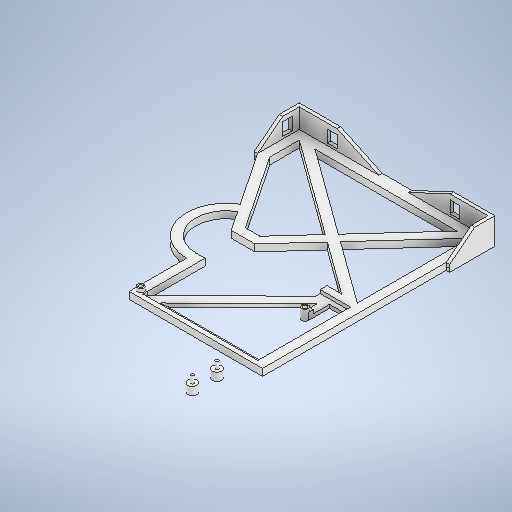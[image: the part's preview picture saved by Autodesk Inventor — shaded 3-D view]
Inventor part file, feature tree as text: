
AUTODESK INVENTOR PART (.ipt)
format: ipt  version: 2025.2 (Build 292293000, 293)  size: 659,968 bytes
history: native  units: mm
features: extrude x17, sketch x5
ambient origin geometry x8: Origin, YZ Plane, XZ Plane, XY Plane, X Axis, Y Axis, Z Axis, Center Point
bodies: Solid1 (feature_tree)
feature tree (22):
  sketch  "Sketch1"  dims[d0=82.0mm d1=54.0mm]
  extrude  "Extrusion1"  Depth=54.0mm
  extrude  "Extrusion2"  Depth=3.0mm
  extrude  "Extrusion3"  Depth=2.9mm
  extrude  "Extrusion4"  Depth=1.5mm TaperAngle=0.0deg
  extrude  "Extrusion5"  Depth=12.24mm
  extrude  "Extrusion6"  Depth=4.2mm
  extrude  "Extrusion10"  Depth=5.2mm
  sketch  "Sketch16"  dims[d6=2.9mm d8=12.5mm]
  extrude  "Extrusion11"  Depth=1.0mm
  extrude  "Extrusion12"  Depth=1.5mm TaperAngle=0.0deg
  extrude  "Extrusion13"  Depth=1.5mm TaperAngle=0.0deg
  extrude  "Extrusion14"  Depth=1.5mm TaperAngle=0.0deg
  extrude  "Extrusion15"  Depth=4.5mm
  extrude  "Extrusion16"  Depth=4.5mm
  extrude  "Extrusion17"  Depth=5.5mm
  extrude  "Extrusion18"  Depth=1.0mm
  extrude  "Extrusion19"  Depth=0.5mm
  extrude  "Extrusion20"  Depth=1.5mm TaperAngle=0.0deg
  sketch  "Sketch2"  dims[d2=44.0mm d5=3.0mm]
  sketch  "Sketch25"  dims[d9=2.9mm d10=1.5mm d11=0.0mm]
  sketch  "Sketch26"  dims[d13=10.0mm d14=12.24mm d16=4.2mm d17=5.2mm d18=1.0mm d19=1.5mm d20=0.0mm d22=1.5mm d23=0.0mm d24=1.5mm d25=0.0mm d26=4.5mm d27=4.5mm d28=5.5mm d29=1.0mm d30=13.825495mm d31=1.5mm d32=0.0mm d34=20.0mm d35=16.44mm d36=18.104mm d37=3.0mm d38=0.0mm d76=1.7mm d78=0.0mm d79=0.0mm d80=4.0mm d81=1.3mm d83=2.0mm d84=0.0mm d85=2.0mm d86=0.0mm d87=5.0mm d88=0.0mm d94=90.0deg d95=90.0deg d96=31.0mm d97=4.0mm d98=4.0mm d103=4.0mm d104=4.0mm d105=1.5mm d106=0.0mm d107=1.5mm d108=0.0mm d110=1.8mm d112=4.0mm d113=7.765622mm d114=1.5mm d115=0.0mm d121=23.473586mm d122=23.650304mm d123=13.528693mm d124=13.140289mm d125=90.0deg d126=9.427875mm d127=7.403962mm d128=4.0mm d129=4.0mm d130=25.52254mm d131=11.748234mm d132=25.0mm d133=51.672948mm d134=4.0mm d135=7.2mm d136=1.5mm d137=1.5mm d138=1.5mm d139=0.0mm d140=2.0mm d141=17.152547mm d142=2.0mm d143=7.942341mm d144=7.0mm d146=1.5mm d147=0.0mm d148=1.5mm d149=0.0mm d150=2.0mm d151=1.5mm d152=0.0mm d154=0.5mm d155=58.0mm d116=0.5mm d117=0.872665mm]
